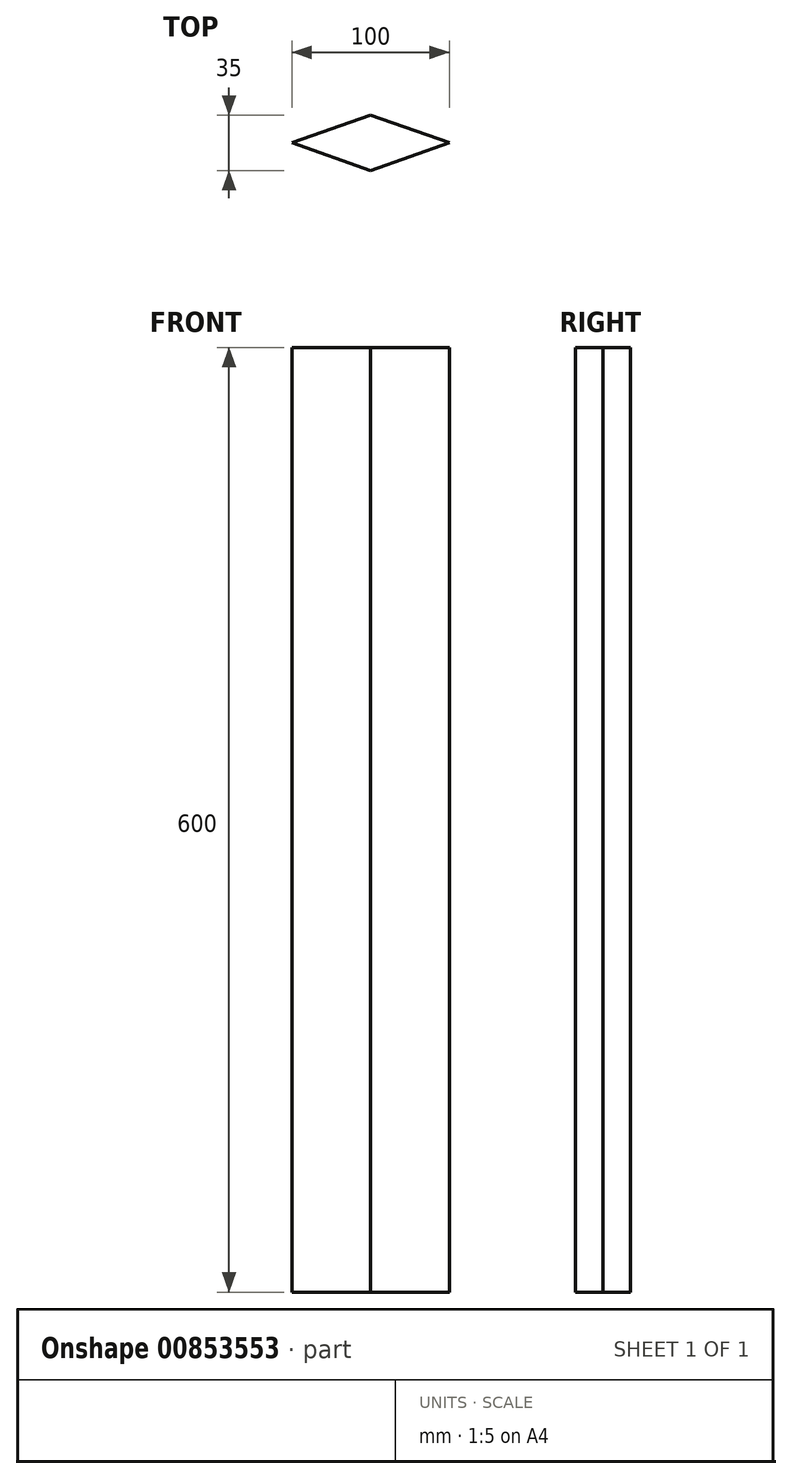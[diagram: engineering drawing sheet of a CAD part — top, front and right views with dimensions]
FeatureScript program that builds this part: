
annotation { "Feature Type Name" : "Feature", "Feature Type Description" : "" }
export const myFeature = defineFeature(function(context is Context, id is Id, definition is map)
    precondition{}
    {
        {
            var Q0;
            Q0=qCreatedBy(makeId("Top.planeOp"),FACE);
            var sketch = newSketch(context, id + "F0", { "sketchPlane" : qUnion([Q0])});
            skLineSegment(sketch, "E0", {"start": v(-50, 0) * mm, "end": v(50, 0) * mm, "construction": true});
            skLineSegment(sketch, "E1", {"start": v(0, 17.5) * mm, "end": v(0, -17.5) * mm, "construction": true});
            skLineSegment(sketch, "E2", {"start": v(-50, 0) * mm, "end": v(0, 17.5) * mm});
            skLineSegment(sketch, "E3", {"start": v(0, 17.5) * mm, "end": v(50, 0) * mm});
            skLineSegment(sketch, "E4", {"start": v(0, -17.5) * mm, "end": v(50, 0) * mm});
            skLineSegment(sketch, "E5", {"start": v(-50, 0) * mm, "end": v(0, -17.5) * mm});
            skSolve(sketch);
        }
        {
            var Q0;
            Q0 = qSketchRegion(id + "F0", true);
            extrude(context, id + "F1", {"entities" : qUnion([Q0]), "depth" : 600 * mm, "offsetDistance" : 25 * mm});
        }
    });
